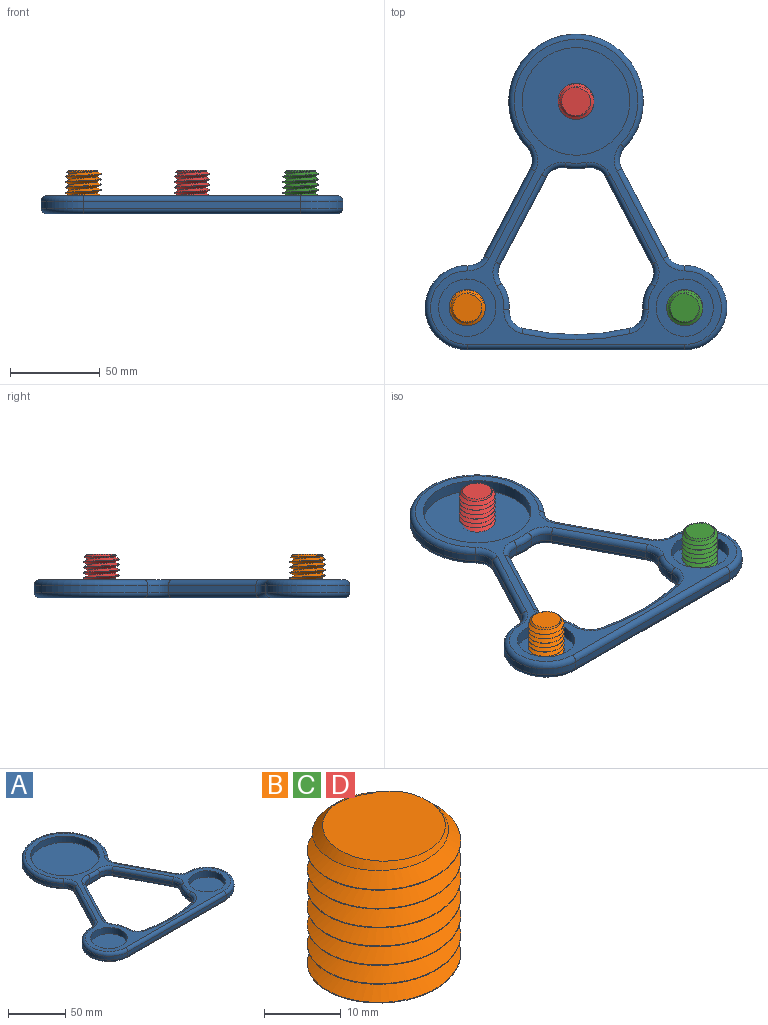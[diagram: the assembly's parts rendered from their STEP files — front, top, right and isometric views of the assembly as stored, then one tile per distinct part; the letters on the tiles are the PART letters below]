
ASSEMBLY  parts=4 mates=3
PART A: 74 faces, bbox 172.1x186.9x10 mm
  f0: plane 48.7x25.67mm, normal (-0.88,-0.47,0), area 220.2mm2, adj f18,f20,f41,f60
  f1: cylinder r=23.5mm len=14.94mm, axis (0,0,-1), area 63.4mm2, adj f18,f19,f42,f63
  f2: cylinder r=130mm len=58.88mm, axis (0,0,-1), area 237.6mm2, adj f19,f24,f46,f59
  f3: cylinder r=23.5mm len=14.94mm, axis (0,0,-1), area 63.4mm2, adj f24,f25,f50,f55
  f4: plane 48.7x25.67mm, normal (0.88,-0.47,0), area 220.2mm2, adj f23,f25,f49,f52
  f5: cylinder r=23.5mm len=47mm, axis (0,0,-1), area 297mm2, adj f13,f17,f33,f68
  f6: plane 48.7x25.67mm, normal (0.88,0.47,0), area 220.2mm2, adj f17,f21,f30,f64
  f7: cylinder r=37.5mm len=75mm, axis (0,0,-1), area 699.9mm2, adj f21,f22,f34,f67
  f8: plane 48.7x25.67mm, normal (-0.88,0.47,0), area 220.2mm2, adj f22,f26,f38,f71
  f9: cylinder r=23.5mm len=47mm, axis (0,0,-1), area 297mm2, adj f13,f26,f37,f72
  f10: cylinder r=30mm len=60mm, axis (0,0,-1), area 1281.8mm2, adj f15,f27
  f11: cylinder r=16mm len=32mm, axis (0,0,-1), area 683.6mm2, adj f15,f29
  f12: cylinder r=37.5mm len=12.08mm, axis (0,0,-1), area 48.5mm2, adj f20,f23,f45,f56
  f13: plane 121.24x4mm, normal (0,-1,0), area 485mm2, adj f5,f9,f35,f70
  f14: cylinder r=16mm len=32mm, axis (0,0,-1), area 683.6mm2, adj f15,f28
  f15: plane 170x162.24mm, normal (0,0,1), area 3293mm2, adj f10,f11,f14,f52,f53,f54,f55,f56
  f16: plane 170x162.24mm, normal (0,0,-1), area 7729mm2, adj f30,f31,f32,f33,f34,f35,f36,f37
  f17: cylinder r=10mm len=9.02mm, axis (0,0,-1), area 44.1mm2, adj f5,f6,f31,f66
  f18: cylinder r=10mm len=10.46mm, axis (0,0,-1), area 44.1mm2, adj f0,f1,f40,f62
  f19: cylinder r=10mm len=10.3mm, axis (0,0,-1), area 55.9mm2, adj f1,f2,f44,f61
  f20: cylinder r=10mm len=10.46mm, axis (0,0,-1), area 49.9mm2, adj f0,f12,f43,f58
  f21: cylinder r=10mm len=11.57mm, axis (0,0,-1), area 49.9mm2, adj f6,f7,f32,f65
  f22: cylinder r=10mm len=11.57mm, axis (0,0,-1), area 49.9mm2, adj f7,f8,f36,f69
  f23: cylinder r=10mm len=10.46mm, axis (0,0,-1), area 49.9mm2, adj f4,f12,f47,f54
  f24: cylinder r=10mm len=10.3mm, axis (0,0,-1), area 55.9mm2, adj f2,f3,f48,f57
  f25: cylinder r=10mm len=10.46mm, axis (0,0,-1), area 44.1mm2, adj f3,f4,f51,f53
  f26: cylinder r=10mm len=9.02mm, axis (0,0,-1), area 44.1mm2, adj f8,f9,f39,f73
  f27: plane 60x60mm, normal (0,0,1), area 2827.4mm2, adj f10
  f28: plane 32x32mm, normal (0,0,1), area 804.2mm2, adj f14
  f29: plane 32x32mm, normal (0,0,1), area 804.2mm2, adj f11
  f30: cylinder r=3mm len=50.1mm, axis (-0.47,0.88,0), area 259.4mm2, adj f6,f16,f31,f32
  f31: torus R=13mm, axis (0,0,1), area 57.7mm2, adj f16,f17,f30,f33
  f32: torus R=13mm, axis (0,0,1), area 65.2mm2, adj f16,f21,f30,f34
  f33: torus R=20.5mm, axis (0,0,1), area 333.6mm2, adj f5,f16,f31,f35
  f34: torus R=34.5mm, axis (0,0,1), area 800.6mm2, adj f7,f16,f32,f36
  f35: cylinder r=3mm len=121.24mm, axis (1,0,0), area 571.3mm2, adj f13,f16,f33,f37
  f36: torus R=13mm, axis (0,0,1), area 65.2mm2, adj f16,f22,f34,f38
  f37: torus R=20.5mm, axis (0,0,1), area 333.6mm2, adj f9,f16,f35,f39
  f38: cylinder r=3mm len=50.1mm, axis (-0.47,-0.88,0), area 259.4mm2, adj f8,f16,f36,f39
  f39: torus R=13mm, axis (0,0,1), area 57.7mm2, adj f16,f26,f37,f38
  f40: torus R=13mm, axis (0,0,1), area 57.7mm2, adj f16,f18,f41,f42
  f41: cylinder r=3mm len=50.1mm, axis (0.47,-0.88,0), area 259.4mm2, adj f0,f16,f40,f43
  f42: torus R=20.5mm, axis (0,0,1), area 71.2mm2, adj f1,f16,f40,f44
  f43: torus R=13mm, axis (0,0,1), area 65.2mm2, adj f16,f20,f41,f45
  f44: torus R=13mm, axis (0,0,1), area 73.1mm2, adj f16,f19,f42,f46
  f45: torus R=34.5mm, axis (0,0,1), area 55.5mm2, adj f12,f16,f43,f47
  f46: torus R=133mm, axis (0,0,1), area 282.2mm2, adj f2,f16,f44,f48
  f47: torus R=13mm, axis (0,0,1), area 65.2mm2, adj f16,f23,f45,f49
  f48: torus R=13mm, axis (0,0,1), area 73.1mm2, adj f16,f24,f46,f50
  f49: cylinder r=3mm len=50.1mm, axis (0.47,0.88,0), area 259.4mm2, adj f4,f16,f47,f51
  f50: torus R=20.5mm, axis (0,0,1), area 71.2mm2, adj f3,f16,f48,f51
  f51: torus R=13mm, axis (0,0,1), area 57.7mm2, adj f16,f25,f49,f50
  f52: cylinder r=3mm len=50.1mm, axis (-0.47,-0.88,0), area 259.4mm2, adj f4,f15,f53,f54
  f53: torus R=13mm, axis (0,0,1), area 57.7mm2, adj f15,f25,f52,f55
  f54: torus R=13mm, axis (0,0,1), area 65.2mm2, adj f15,f23,f52,f56
  f55: torus R=20.5mm, axis (0,0,1), area 71.2mm2, adj f3,f15,f53,f57
  f56: torus R=34.5mm, axis (0,0,1), area 55.5mm2, adj f12,f15,f54,f58
  f57: torus R=13mm, axis (0,0,1), area 73.1mm2, adj f15,f24,f55,f59
  f58: torus R=13mm, axis (0,0,1), area 65.2mm2, adj f15,f20,f56,f60
  f59: torus R=133mm, axis (0,0,1), area 282.2mm2, adj f2,f15,f57,f61
  f60: cylinder r=3mm len=50.1mm, axis (-0.47,0.88,0), area 259.4mm2, adj f0,f15,f58,f62
  f61: torus R=13mm, axis (0,0,1), area 73.1mm2, adj f15,f19,f59,f63
  f62: torus R=13mm, axis (0,0,1), area 57.7mm2, adj f15,f18,f60,f63
  f63: torus R=20.5mm, axis (0,0,1), area 71.2mm2, adj f1,f15,f61,f62
  f64: cylinder r=3mm len=50.1mm, axis (0.47,-0.88,0), area 259.4mm2, adj f6,f15,f65,f66
  f65: torus R=13mm, axis (0,0,1), area 65.2mm2, adj f15,f21,f64,f67
  f66: torus R=13mm, axis (0,0,1), area 57.7mm2, adj f15,f17,f64,f68
  f67: torus R=34.5mm, axis (0,0,1), area 800.6mm2, adj f7,f15,f65,f69
  f68: torus R=20.5mm, axis (0,0,1), area 333.6mm2, adj f5,f15,f66,f70
  f69: torus R=13mm, axis (0,0,1), area 65.2mm2, adj f15,f22,f67,f71
  f70: cylinder r=3mm len=121.24mm, axis (-1,0,0), area 571.3mm2, adj f13,f15,f68,f72
  f71: cylinder r=3mm len=50.1mm, axis (0.47,0.88,0), area 259.4mm2, adj f8,f15,f69,f73
  f72: torus R=20.5mm, axis (0,0,1), area 333.6mm2, adj f9,f15,f70,f73
  f73: torus R=13mm, axis (0,0,1), area 57.7mm2, adj f15,f26,f71,f72
PART B: 6 faces, bbox 22x25.1x27.5 mm
  f0: cylinder r=10mm len=20mm, axis (0,0,-1), area -70.8mm2, adj f2,f3,f4,f5
  f1: plane 16.18x16.07mm, normal (0,0,1), area 198.6mm2, adj f3,f4,f5
  f2: plane 19.72x19.7mm, normal (0,0,-1), area 244.2mm2, adj f0,f4,f5
  f3: cone r=8mm half-angle=45deg, axis (0,0,-1), area 64.7mm2, adj f0,f1,f4,f5
  f4: bspline ~23.95x23.09mm, area 1129.6mm2, adj f0,f1,f2,f3,f5
  f5: bspline ~25.45x23.09mm, area 1124.5mm2, adj f0,f1,f2,f3,f4
PART C: same geometry as B
PART D: same geometry as B
PLACE A t=(-36.02,-76.29,1.71)mm
PLACE B t=(-96.64,-76.29,3.91)mm
PLACE C t=(24.6,-76.29,3.91)mm
PLACE D t=(-36.02,38.71,3.91)mm
MATE fastened C.f0 <-> A.f1  axis (0,0,-1) through (24.6,-76.29,3.91)mm
MATE fastened B.f0 <-> A.f3  axis (0,0,-1) through (-96.64,-76.29,3.91)mm
MATE fastened D.f0 <-> A.f10  axis (0,0,-1) through (-36.02,38.71,3.91)mm
